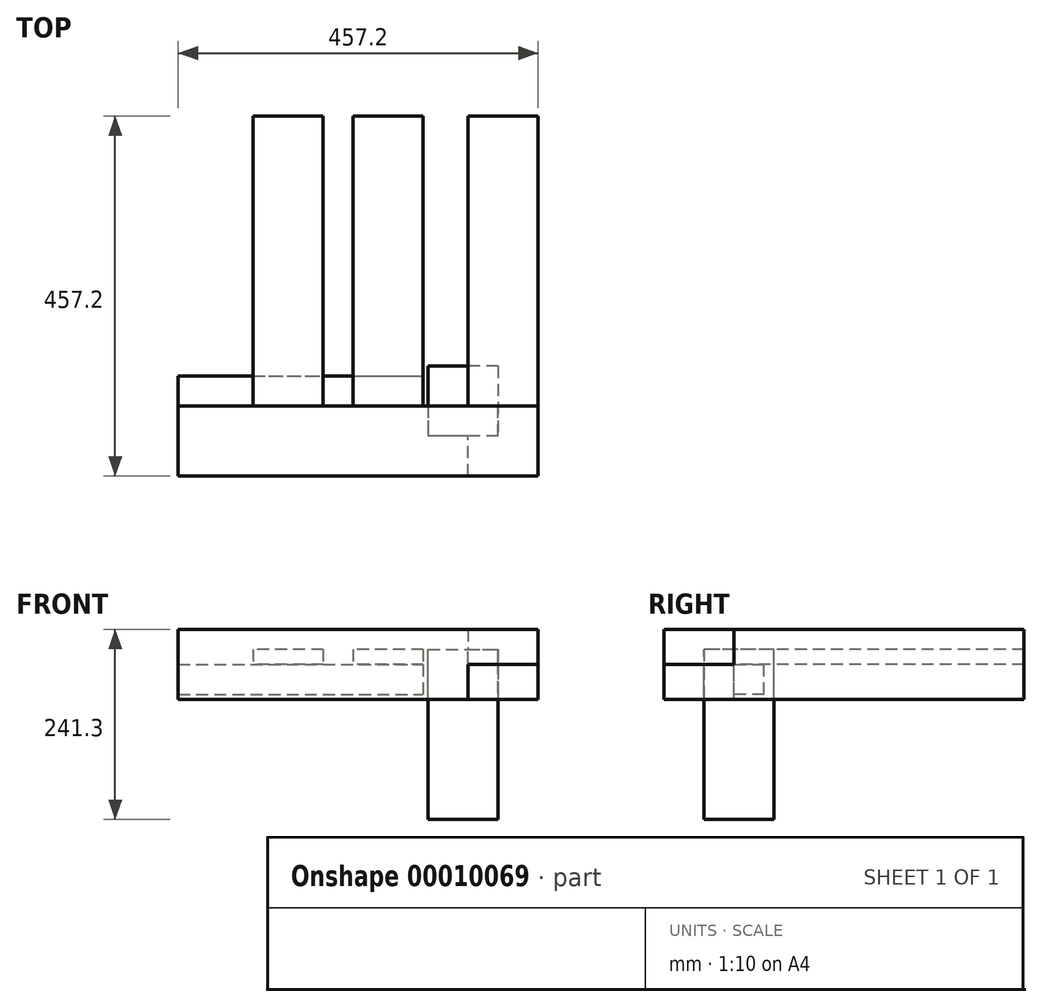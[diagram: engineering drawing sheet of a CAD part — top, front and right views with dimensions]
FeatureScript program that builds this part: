
annotation { "Feature Type Name" : "Feature", "Feature Type Description" : "" }
export const myFeature = defineFeature(function(context is Context, id is Id, definition is map)
    precondition{}
    {
        {
            var Q0;
            Q0=qCreatedBy(makeId("Front.planeOp"),FACE);
            var sketch = newSketch(context, id + "F0", { "sketchPlane" : qUnion([Q0])});
            skLineSegment(sketch, "E0", {"start": v(0, 0) * mm, "end": v(0, 44.45) * mm});
            skLineSegment(sketch, "E1", {"start": v(0, 44.45) * mm, "end": v(-457.2, 44.45) * mm});
            skLineSegment(sketch, "E2", {"start": v(-457.2, 44.45) * mm, "end": v(-457.2, -44.45) * mm});
            skLineSegment(sketch, "E3", {"start": v(-457.2, -44.45) * mm, "end": v(-88.9, -44.45) * mm});
            skLineSegment(sketch, "E4", {"start": v(-88.9, -44.45) * mm, "end": v(-88.9, 0) * mm});
            skLineSegment(sketch, "E5", {"start": v(-88.9, 0) * mm, "end": v(0, 0) * mm});
            skSolve(sketch);
        }
        {
            var Q0;
            Q0=makeQuery(id+"F0.imprint","IMPRINT",FACE,{"disambiguationData":[TD([[makeQuery(id+"F0.imprint","IMPRINT",EDGE,{"derivedFrom":sQuery(id+"F0.wireOp",EDGE,"E0")}),1.0]])]});
            extrude(context, id + "F1", {"entities" : qUnion([Q0]), "depth" : 88.9 * mm});
        }
        {
            var Q0;
            Q0=qCreatedBy(makeId("Right.planeOp"),FACE);
            var sketch = newSketch(context, id + "F2", { "sketchPlane" : qUnion([Q0])});
            skLineSegment(sketch, "E6", {"start": v(0, 0) * mm, "end": v(-88.9, 0) * mm});
            skLineSegment(sketch, "E7", {"start": v(-88.9, 0) * mm, "end": v(-88.9, -44.45) * mm});
            skLineSegment(sketch, "E8", {"start": v(-88.9, -44.45) * mm, "end": v(368.3, -44.45) * mm});
            skLineSegment(sketch, "E9", {"start": v(368.3, -44.45) * mm, "end": v(368.3, 44.45) * mm});
            skLineSegment(sketch, "E10", {"start": v(368.3, 44.45) * mm, "end": v(0, 44.45) * mm});
            skLineSegment(sketch, "E11", {"start": v(0, 44.45) * mm, "end": v(0, 0) * mm});
            skSolve(sketch);
        }
        {
            var Q0;
            Q0=makeQuery(id+"F2.imprint","IMPRINT",FACE,{"disambiguationData":[TD([[makeQuery(id+"F2.imprint","IMPRINT",EDGE,{"derivedFrom":sQuery(id+"F2.wireOp",EDGE,"E6")}),1.0]])]});
            var Q1;
            Q1=makeQuery(id+"F1.opExtrude","SWEPT_FACE",FACE,{"disambiguationData":[OSD([sQuery(id+"F0.wireOp",EDGE,"E4")])]});
            extrude(context, id + "F3", {"entities" : qUnion([Q0]), "endBound" : BoundingType.UP_TO_SURFACE, "oppositeDirection" : true, "endBoundEntityFace" : qUnion([Q1]), "depth" : 25.4 * mm});
        }
        {
            var Q0;
            Q0=makeQuery(id+"F3.opExtrude","SWEPT_FACE",FACE,{"disambiguationData":[OSD([sQuery(id+"F2.wireOp",EDGE,"E8")])]});
            var sketch = newSketch(context, id + "F4", { "sketchPlane" : qUnion([Q0])});
            skLineSegment(sketch, "E12.bottom", {"start": v(-50.8, -50.8) * mm, "end": v(-139.7, -50.8) * mm});
            skLineSegment(sketch, "E12.top", {"start": v(-50.8, 38.1) * mm, "end": v(-139.7, 38.1) * mm});
            skLineSegment(sketch, "E12.left", {"start": v(-50.8, -50.8) * mm, "end": v(-50.8, 38.1) * mm});
            skLineSegment(sketch, "E12.right", {"start": v(-139.7, -50.8) * mm, "end": v(-139.7, 38.1) * mm});
            skSolve(sketch);
        }
        {
            var Q0;
            {var subQ5=sQuery(id+"F4.wireOp",EDGE,"E12.left");Q0=makeQuery(id+"F4.imprint","IMPRINT",FACE,{"disambiguationData":[TD([[makeQuery(id+"F4.imprint","IMPRINT",EDGE,{"derivedFrom":subQ5}),1.0]])]});}
            var Q1;
            {var subQ5=sQuery(id+"F4.wireOp",EDGE,"E12.right");Q1=makeQuery(id+"F4.imprint","IMPRINT",FACE,{"disambiguationData":[TD([[makeQuery(id+"F4.imprint","IMPRINT",EDGE,{"derivedFrom":subQ5}),-1.0]])]});}
            extrude(context, id + "F5", {"entities" : qUnion([Q0, Q1]), "operationType" : NewBodyOperationType.REMOVE, "oppositeDirection" : true, "depth" : 63.5 * mm});
        }
        {
            var Q0;
            {var subQ5=sQuery(id+"F4.wireOp",EDGE,"E12.right");Q0=makeQuery(id+"F4.imprint","IMPRINT",FACE,{"disambiguationData":[TD([[makeQuery(id+"F4.imprint","IMPRINT",EDGE,{"derivedFrom":subQ5}),-1.0]])]});}
            var Q1;
            {var subQ5=sQuery(id+"F4.wireOp",EDGE,"E12.left");Q1=makeQuery(id+"F4.imprint","IMPRINT",FACE,{"disambiguationData":[TD([[makeQuery(id+"F4.imprint","IMPRINT",EDGE,{"derivedFrom":subQ5}),1.0]])]});}
            var Q2;
            Q2=makeQuery(id+"F5.boolean.opBoolean","COPY",FACE,{"disambiguationData":[OD(0.0)],"derivedFrom":makeQuery(id+"F5.opExtrude","CAP_FACE",FACE,{"disambiguationData":[OSD([sQuery(id+"F4.wireOp",EDGE,"E12.bottom"),sQuery(id+"F4.wireOp",EDGE,"E12.top"),sQuery(id+"F4.wireOp",EDGE,"E12.left"),sQuery(id+"F4.wireOp",EDGE,"E12.right")])],"isStart":false})});
            extrude(context, id + "F6", {"entities" : qUnion([Q0, Q1]), "depth" : 152.4 * mm, "hasSecondDirection" : true, "secondDirectionBound" : SecondDirectionBoundingType.UP_TO_SURFACE, "secondDirectionOppositeDirection" : true, "secondDirectionBoundEntityFace" : qUnion([Q2]), "secondDirectionDepth" : 25.4 * mm});
        }
        {
            var Q0;
            Q0=makeQuery(id+"F1.opExtrude","CAP_FACE",FACE,{"disambiguationData":[OSD([sQuery(id+"F0.wireOp",EDGE,"E0"),sQuery(id+"F0.wireOp",EDGE,"E1"),sQuery(id+"F0.wireOp",EDGE,"E2"),sQuery(id+"F0.wireOp",EDGE,"E3"),sQuery(id+"F0.wireOp",EDGE,"E4"),sQuery(id+"F0.wireOp",EDGE,"E5")])],"isStart":true});
            var sketch = newSketch(context, id + "F7", { "sketchPlane" : qUnion([Q0])});
            skLineSegment(sketch, "E13.bottom", {"start": v(146.05, 19.05) * mm, "end": v(234.95, 19.05) * mm});
            skLineSegment(sketch, "E13.top", {"start": v(146.05, 0) * mm, "end": v(234.95, 0) * mm});
            skLineSegment(sketch, "E13.left", {"start": v(146.05, 19.05) * mm, "end": v(146.05, 0) * mm});
            skLineSegment(sketch, "E13.right", {"start": v(234.95, 19.05) * mm, "end": v(234.95, 0) * mm});
            skLineSegment(sketch, "E14.1.0.0", {"start": v(273.05, 0) * mm, "end": v(361.95, 0) * mm});
            skLineSegment(sketch, "E14.1.0.1", {"start": v(273.05, 19.05) * mm, "end": v(361.95, 19.05) * mm});
            skLineSegment(sketch, "E14.1.0.2", {"start": v(361.95, 19.05) * mm, "end": v(361.95, 0) * mm});
            skLineSegment(sketch, "E14.1.0.3", {"start": v(273.05, 19.05) * mm, "end": v(273.05, 0) * mm});
            skLineSegment(sketch, "E14.direction1", {"start": v(146.05, 0) * mm, "end": v(273.05, 0) * mm, "construction": true});
            skSolve(sketch);
        }
        {
            var Q0;
            Q0=makeQuery(id+"F7.imprint","IMPRINT",FACE,{"disambiguationData":[TD([[makeQuery(id+"F7.imprint","IMPRINT",EDGE,{"derivedFrom":sQuery(id+"F7.wireOp",EDGE,"E13.bottom")}),-1.0]])]});
            var Q1;
            Q1=makeQuery(id+"F7.imprint","IMPRINT",FACE,{"disambiguationData":[TD([[makeQuery(id+"F7.imprint","IMPRINT",EDGE,{"derivedFrom":sQuery(id+"F7.wireOp",EDGE,"E14.1.0.0")}),1.0]])]});
            var Q2;
            Q2=makeQuery(id+"F3.opExtrude","SWEPT_FACE",FACE,{"disambiguationData":[OSD([sQuery(id+"F2.wireOp",EDGE,"E9")])]});
            extrude(context, id + "F8", {"entities" : qUnion([Q0, Q1]), "endBound" : BoundingType.UP_TO_SURFACE, "endBoundEntityFace" : qUnion([Q2]), "depth" : 25.4 * mm});
        }
        {
            var Q0;
            Q0=makeQuery(id+"F8.opExtrude","SWEPT_FACE",FACE,{"disambiguationData":[OSD([sQuery(id+"F7.wireOp",EDGE,"E13.left")])]});
            var sketch = newSketch(context, id + "F9", { "sketchPlane" : qUnion([Q0])});
            skLineSegment(sketch, "E15.bottom", {"start": v(0, 0) * mm, "end": v(38.1, 0) * mm});
            skLineSegment(sketch, "E15.top", {"start": v(0, -38.1) * mm, "end": v(38.1, -38.1) * mm});
            skLineSegment(sketch, "E15.left", {"start": v(0, 0) * mm, "end": v(0, -38.1) * mm});
            skLineSegment(sketch, "E15.right", {"start": v(38.1, 0) * mm, "end": v(38.1, -38.1) * mm});
            skSolve(sketch);
        }
        {
            var Q0;
            Q0=makeQuery(id+"F9.imprint","IMPRINT",FACE,{"disambiguationData":[TD([[makeQuery(id+"F9.imprint","IMPRINT",EDGE,{"derivedFrom":sQuery(id+"F9.wireOp",EDGE,"E15.bottom")}),1.0]])]});
            var Q1;
            Q1=makeQuery(id+"F1.opExtrude","SWEPT_FACE",FACE,{"disambiguationData":[OSD([sQuery(id+"F0.wireOp",EDGE,"E2")])]});
            extrude(context, id + "F10", {"entities" : qUnion([Q0]), "endBound" : BoundingType.UP_TO_SURFACE, "oppositeDirection" : true, "endBoundEntityFace" : qUnion([Q1]), "depth" : 25.4 * mm});
        }
    });
